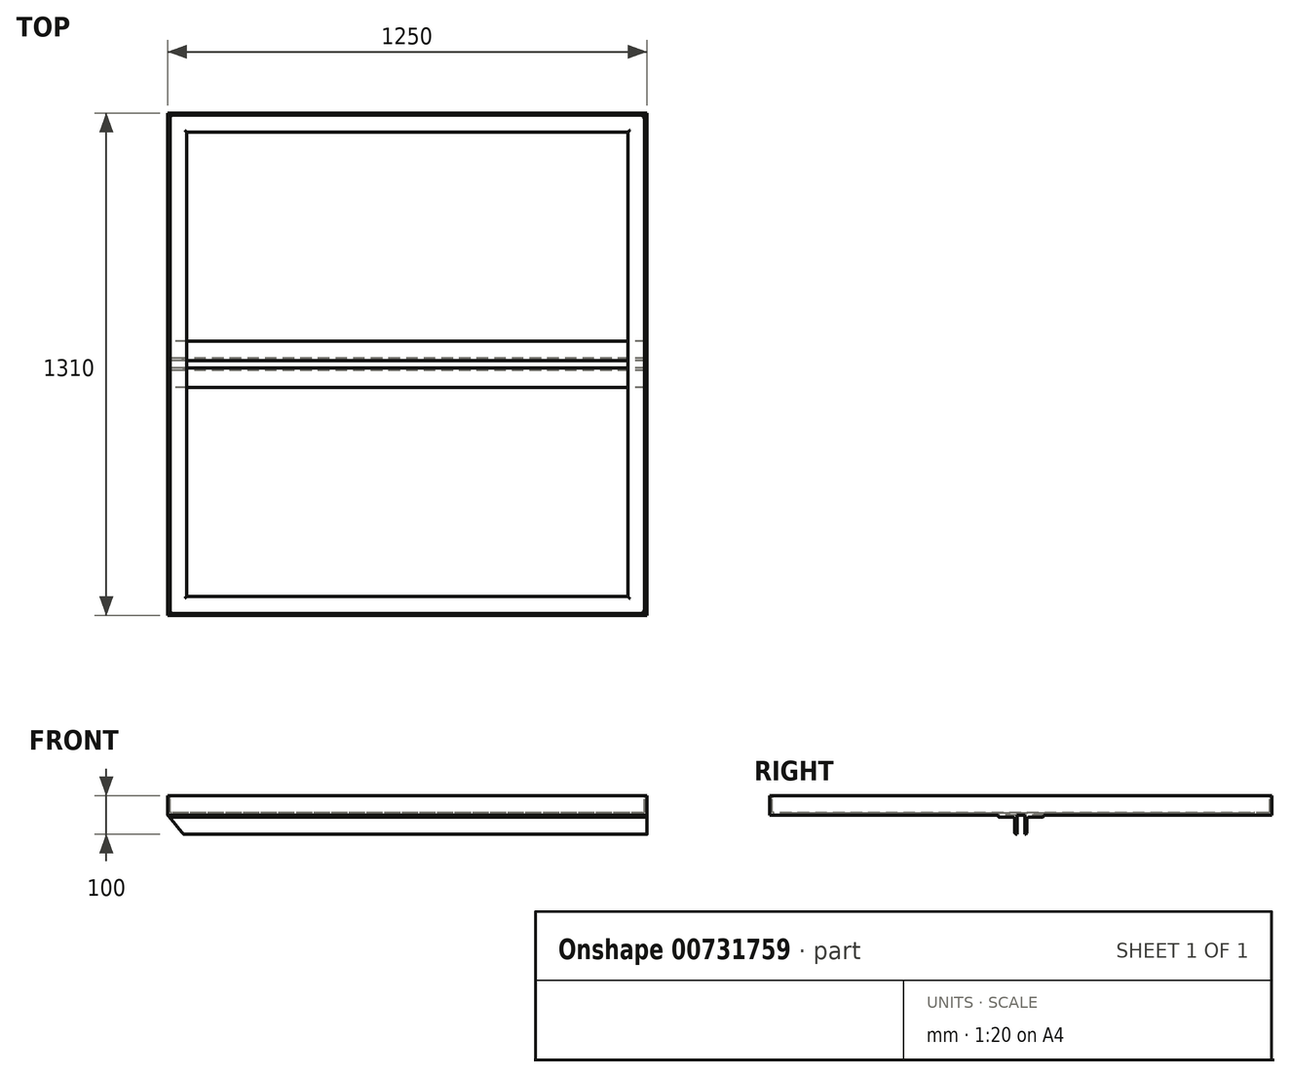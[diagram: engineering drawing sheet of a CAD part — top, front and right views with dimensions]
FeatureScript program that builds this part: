
annotation { "Feature Type Name" : "Feature", "Feature Type Description" : "" }
export const myFeature = defineFeature(function(context is Context, id is Id, definition is map)
    precondition{}
    {
        {
            var Q0;
            Q0=qCreatedBy(makeId("Top.planeOp"),FACE);
            var sketch = newSketch(context, id + "F0", { "sketchPlane" : qUnion([Q0])});
            skLineSegment(sketch, "E0.bottom", {"start": v(0, 0) * mm, "end": v(1250, 0) * mm});
            skLineSegment(sketch, "E0.top", {"start": v(0, 1310) * mm, "end": v(1250, 1310) * mm});
            skLineSegment(sketch, "E0.left", {"start": v(0, 0) * mm, "end": v(0, 1310) * mm});
            skLineSegment(sketch, "E0.right", {"start": v(1250, 0) * mm, "end": v(1250, 1310) * mm});
            skSolve(sketch);
        }
        {
            var Q0;
            Q0=qCreatedBy(makeId("Front.planeOp"),FACE);
            var sketch = newSketch(context, id + "F1", { "sketchPlane" : qUnion([Q0])});
            skLineSegment(sketch, "E1.bottom", {"start": v(0, 0) * mm, "end": v(50, 0) * mm});
            skLineSegment(sketch, "E1.top", {"start": v(0, 50) * mm, "end": v(1, 50) * mm});
            skLineSegment(sketch, "E1.left", {"start": v(0, 0) * mm, "end": v(0, 50) * mm});
            skLineSegment(sketch, "E1.right", {"start": v(50, 0) * mm, "end": v(50, 1) * mm});
            skLineSegment(sketch, "E2.0", {"start": v(6, 11) * mm, "end": v(6, 45) * mm});
            skLineSegment(sketch, "E2.1", {"start": v(11, 6) * mm, "end": v(45, 6) * mm});
            skPoint(sketch, "E3.visualSharp", {"position": v(6, 50) * mm});
            skArc(sketch, "E3.filletArc", {"start": v(6, 45) * mm, "mid": v(4.54, 48.54) * mm, "end": v(1, 50) * mm});
            skPoint(sketch, "E4.visualSharp", {"position": v(50, 6) * mm});
            skArc(sketch, "E4.filletArc", {"start": v(50, 1) * mm, "mid": v(48.54, 4.54) * mm, "end": v(45, 6) * mm});
            skPoint(sketch, "E5.visualSharp", {"position": v(6, 6) * mm});
            skArc(sketch, "E5.filletArc", {"start": v(6, 11) * mm, "mid": v(7.46, 7.46) * mm, "end": v(11, 6) * mm});
            skSolve(sketch);
        }
        {
            var Q0;
            Q0 = qSketchRegion(id + "F1", true);
            var Q1;
            Q1 = qConstructionFilter(qBodyType(qCreatedBy(id + "F0" ,EDGE), BodyType.WIRE), ConstructionObject.NO);
            sweep(context, id + "F2", {"profiles" : qUnion([Q0]), "path" : qUnion([Q1])});
        }
        {
            var Q0;
            Q0=makeQuery(id+"F2.opSweep","SWEPT_FACE",FACE,{"disambiguationData":[OSD([sQuery(id+"F0.wireOp",EDGE,"E0.top"),sQuery(id+"F1.wireOp",EDGE,"E1.left")])]});
            var sketch = newSketch(context, id + "F3", { "sketchPlane" : qUnion([Q0])});
            skCircle(sketch, "E6", {"center": v(-1230, 20) * mm, "radius": 19 * mm});
            skSolve(sketch);
        }
        {
            var Q0;
            Q0=makeQuery(id+"F2.opSweep","SWEPT_FACE",FACE,{"disambiguationData":[OSD([sQuery(id+"F0.wireOp",EDGE,"E0.bottom"),sQuery(id+"F1.wireOp",EDGE,"E1.left")])]});
            var sketch = newSketch(context, id + "F4", { "sketchPlane" : qUnion([Q0])});
            skCircle(sketch, "E7", {"center": v(1230, 20) * mm, "radius": 19 * mm});
            skSolve(sketch);
        }
        {
            var Q0;
            Q0=qCreatedBy(makeId("Right.planeOp"),FACE);
            var sketch = newSketch(context, id + "F5", { "sketchPlane" : qUnion([Q0])});
            skLineSegment(sketch, "E8.bottom", {"start": v(645, 0) * mm, "end": v(595, 0) * mm});
            skLineSegment(sketch, "E8.top", {"start": v(645, -50) * mm, "end": v(644, -50) * mm});
            skLineSegment(sketch, "E8.left", {"start": v(645, 0) * mm, "end": v(645, -50) * mm});
            skLineSegment(sketch, "E8.right", {"start": v(595, 0) * mm, "end": v(595, -1) * mm});
            skLineSegment(sketch, "E9.0", {"start": v(639, -11) * mm, "end": v(639, -45) * mm});
            skLineSegment(sketch, "E9.1", {"start": v(634, -6) * mm, "end": v(600, -6) * mm});
            skPoint(sketch, "E10.visualSharp", {"position": v(639, -50) * mm});
            skArc(sketch, "E10.filletArc", {"start": v(639, -45) * mm, "mid": v(640.46, -48.54) * mm, "end": v(644, -50) * mm});
            skPoint(sketch, "E11.visualSharp", {"position": v(595, -6) * mm});
            skArc(sketch, "E11.filletArc", {"start": v(595, -1) * mm, "mid": v(596.46, -4.54) * mm, "end": v(600, -6) * mm});
            skPoint(sketch, "E12.visualSharp", {"position": v(639, -6) * mm});
            skArc(sketch, "E12.filletArc", {"start": v(639, -11) * mm, "mid": v(637.54, -7.46) * mm, "end": v(634, -6) * mm});
            skLineSegment(sketch, "E13", {"start": v(655, 0) * mm, "end": v(655, -78.2) * mm, "construction": true});
            skLineSegment(sketch, "E14.MirrorCS", {"start": v(665, -50) * mm, "end": v(666, -50) * mm});
            skArc(sketch, "E15.MirrorCS", {"start": v(671, -11) * mm, "mid": v(672.46, -7.46) * mm, "end": v(676, -6) * mm});
            skArc(sketch, "E16.MirrorCS", {"start": v(671, -45) * mm, "mid": v(669.54, -48.54) * mm, "end": v(666, -50) * mm});
            skLineSegment(sketch, "E17.MirrorCS", {"start": v(715, 0) * mm, "end": v(715, -1) * mm});
            skArc(sketch, "E18.MirrorCS", {"start": v(715, -1) * mm, "mid": v(713.54, -4.54) * mm, "end": v(710, -6) * mm});
            skPoint(sketch, "E19.MirrorP", {"position": v(671, -50) * mm});
            skPoint(sketch, "E20.MirrorP", {"position": v(715, -6) * mm});
            skLineSegment(sketch, "E21.MirrorCS", {"start": v(676, -6) * mm, "end": v(710, -6) * mm});
            skLineSegment(sketch, "E22.MirrorCS", {"start": v(671, -11) * mm, "end": v(671, -45) * mm});
            skLineSegment(sketch, "E23.MirrorCS", {"start": v(665, 0) * mm, "end": v(665, -50) * mm});
            skLineSegment(sketch, "E24.MirrorCS", {"start": v(665, 0) * mm, "end": v(715, 0) * mm});
            skPoint(sketch, "E25.MirrorP", {"position": v(671, -6) * mm});
            skSolve(sketch);
        }
        {
            var Q0;
            Q0 = qSketchRegion(id + "F5", true);
            var Q1;
            Q1=makeQuery(id+"F2.opSweep","SWEPT_FACE",FACE,{"disambiguationData":[OSD([sQuery(id+"F0.wireOp",EDGE,"E0.right"),sQuery(id+"F1.wireOp",EDGE,"E1.left")])]});
            extrude(context, id + "F6", {"entities" : qUnion([Q0]), "operationType" : NewBodyOperationType.ADD, "endBound" : BoundingType.UP_TO_SURFACE, "depth" : 25 * mm, "endBoundEntityFace" : qUnion([Q1]), "offsetDistance" : 25 * mm});
        }
        {
            var Q0;
            Q0=makeQuery(id+"F2.opSweep","SWEPT_FACE",FACE,{"disambiguationData":[OSD([sQuery(id+"F0.wireOp",EDGE,"E0.bottom"),sQuery(id+"F1.wireOp",EDGE,"E1.left")])]});
            var sketch = newSketch(context, id + "F7", { "sketchPlane" : qUnion([Q0])});
            skLineSegment(sketch, "E26.bottom", {"start": v(1244, 0) * mm, "end": v(1206, 0) * mm});
            skLineSegment(sketch, "E26.top", {"start": v(1244, 50) * mm, "end": v(1206, 50) * mm});
            skLineSegment(sketch, "E26.left", {"start": v(1250, 6) * mm, "end": v(1250, 44) * mm});
            skLineSegment(sketch, "E26.right", {"start": v(1200, 6) * mm, "end": v(1200, 44) * mm});
            skPoint(sketch, "E27.visualSharp", {"position": v(1200, 50) * mm});
            skArc(sketch, "E27.filletArc", {"start": v(1206, 50) * mm, "mid": v(1201.76, 48.24) * mm, "end": v(1200, 44) * mm});
            skPoint(sketch, "E28.visualSharp", {"position": v(1250, 50) * mm});
            skArc(sketch, "E28.filletArc", {"start": v(1250, 44) * mm, "mid": v(1248.24, 48.24) * mm, "end": v(1244, 50) * mm});
            skPoint(sketch, "E29.visualSharp", {"position": v(1250, 0) * mm});
            skArc(sketch, "E29.filletArc", {"start": v(1244, 0) * mm, "mid": v(1248.24, 1.76) * mm, "end": v(1250, 6) * mm});
            skPoint(sketch, "E30.visualSharp", {"position": v(1200, 0) * mm});
            skArc(sketch, "E30.filletArc", {"start": v(1200, 6) * mm, "mid": v(1201.76, 1.76) * mm, "end": v(1206, 0) * mm});
            skArc(sketch, "E31.0", {"start": v(1247, 44) * mm, "mid": v(1246.12, 46.12) * mm, "end": v(1244, 47) * mm});
            skLineSegment(sketch, "E31.1", {"start": v(1247, 6) * mm, "end": v(1247, 44) * mm});
            skLineSegment(sketch, "E31.2", {"start": v(1244, 47) * mm, "end": v(1206, 47) * mm});
            skArc(sketch, "E31.3", {"start": v(1244, 3) * mm, "mid": v(1246.12, 3.88) * mm, "end": v(1247, 6) * mm});
            skArc(sketch, "E31.4", {"start": v(1206, 47) * mm, "mid": v(1203.88, 46.12) * mm, "end": v(1203, 44) * mm});
            skLineSegment(sketch, "E31.5", {"start": v(1203, 6) * mm, "end": v(1203, 44) * mm});
            skArc(sketch, "E31.6", {"start": v(1203, 6) * mm, "mid": v(1203.88, 3.88) * mm, "end": v(1206, 3) * mm});
            skLineSegment(sketch, "E31.7", {"start": v(1244, 3) * mm, "end": v(1206, 3) * mm});
            skSolve(sketch);
        }
        {
            var Q0;
            Q0=makeQuery(id+"F2.opSweep","SWEPT_FACE",FACE,{"disambiguationData":[OSD([sQuery(id+"F0.wireOp",EDGE,"E0.bottom"),sQuery(id+"F1.wireOp",EDGE,"E1.left")])]});
            var sketch = newSketch(context, id + "F8", { "sketchPlane" : qUnion([Q0])});
            skLineSegment(sketch, "E32", {"start": v(0, 0) * mm, "end": v(0, -60) * mm});
            skLineSegment(sketch, "E33", {"start": v(0, 0) * mm, "end": v(50, -60) * mm});
            skLineSegment(sketch, "E34", {"start": v(50, -60) * mm, "end": v(0, -60) * mm});
            skSolve(sketch);
        }
        {
            var Q0;
            Q0 = qSketchRegion(id + "F8", true);
            var Q1;
            Q1=makeQuery(id+"F2.opSweep","SWEPT_FACE",FACE,{"disambiguationData":[OSD([sQuery(id+"F0.wireOp",EDGE,"E0.top"),sQuery(id+"F1.wireOp",EDGE,"E1.left")])]});
            extrude(context, id + "F9", {"entities" : qUnion([Q0]), "operationType" : NewBodyOperationType.REMOVE, "endBound" : BoundingType.UP_TO_SURFACE, "oppositeDirection" : true, "depth" : 25 * mm, "endBoundEntityFace" : qUnion([Q1]), "offsetDistance" : 25 * mm});
        }
    });
